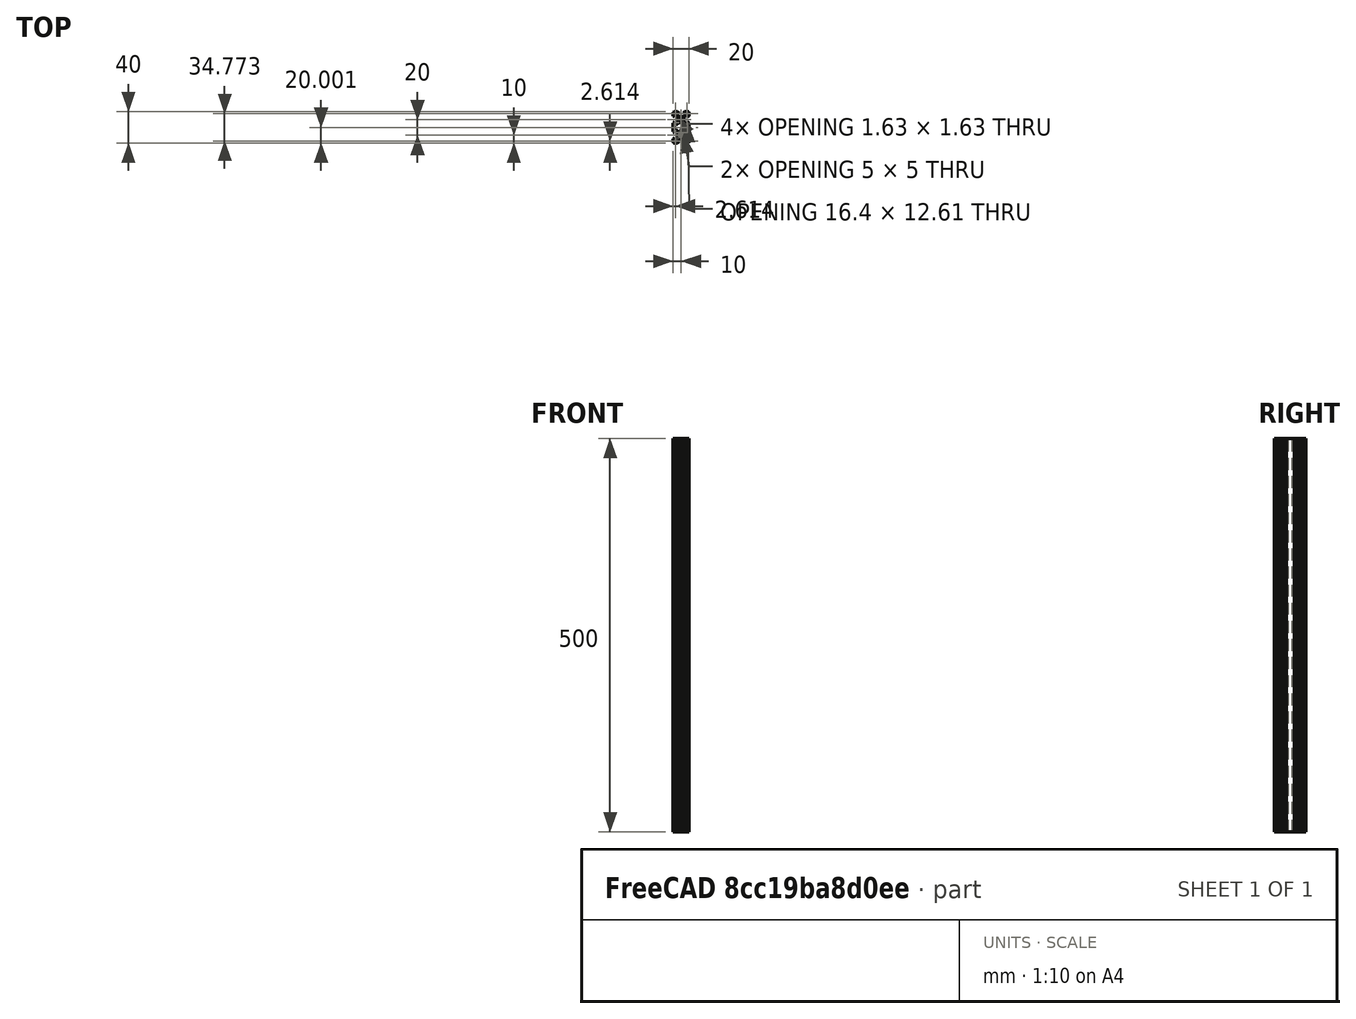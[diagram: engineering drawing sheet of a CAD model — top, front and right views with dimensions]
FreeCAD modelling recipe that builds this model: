
FCSTD DOCUMENT  (FreeCAD 0.16R6707 (Git))
Label: extrusion 20mmx40mm
License: All rights reserved
LicenseURL: http://en.wikipedia.org/wiki/All_rights_reserved
objects: Sketcher::SketchObject×1, PartDesign::Pad×1
note: 3 computed .brp shape members not serialized (recipe doc carries the construction recipe); baked Part::Feature solids carry a one-line shape summary decoded from their .brp

FEATURE [Sketcher::SketchObject] Sketch
  sketch-geometry (372):
    g0: LineSegment StartX=9.79303 StartY=6.1 StartZ=0 EndX=7.16067 EndY=6.1 EndZ=0
    g1: LineSegment StartX=10 StartY=6.30697 StartZ=0 EndX=9.79303 EndY=6.1 EndZ=0
    g2: LineSegment StartX=7.16067 StartY=6.1 StartZ=0 EndX=4.5 EndY=3.43934 EndZ=0
    g3: LineSegment StartX=10.207 StartY=6.1 StartZ=0 EndX=10 EndY=6.30697 EndZ=0
    g4: LineSegment StartX=4.5 StartY=3.43934 StartZ=0 EndX=4.5 EndY=1.8 EndZ=0
    g5: LineSegment StartX=12.8393 StartY=6.1 StartZ=0 EndX=10.207 EndY=6.1 EndZ=0
    g6: LineSegment StartX=4.5 StartY=1.8 StartZ=0 EndX=7.11338 EndY=1.8 EndZ=0
    g7: LineSegment StartX=15.5 StartY=3.43934 StartZ=0 EndX=12.8393 EndY=6.1 EndZ=0
    g8: LineSegment StartX=7.11338 StartY=1.8 StartZ=0 EndX=7.11338 EndY=1.69337 EndZ=0
    g9: LineSegment StartX=15.5 StartY=1.8 StartZ=0 EndX=15.5 EndY=3.43934 EndZ=0
    g10: LineSegment StartX=7.11338 StartY=1.69337 StartZ=0 EndX=5.59781 EndY=0.177796 EndZ=0
    g11: LineSegment StartX=12.8866 StartY=1.8 StartZ=0 EndX=15.5 EndY=1.8 EndZ=0
    g12: LineSegment StartX=5.59781 StartY=0.177796 StartZ=0 EndX=5.56881 EndY=0.150641 EndZ=0
    g13: LineSegment StartX=12.8866 StartY=1.69337 StartZ=0 EndX=12.8866 EndY=1.8 EndZ=0
    g14: LineSegment StartX=5.56881 StartY=0.150641 StartZ=0 EndX=5.53811 EndY=0.12544 EndZ=0
    g15: LineSegment StartX=14.4022 StartY=0.177796 StartZ=0 EndX=12.8866 EndY=1.69337 EndZ=0
    g16: LineSegment StartX=5.53811 StartY=0.12544 StartZ=0 EndX=5.50582 EndY=0.102301 EndZ=0
    g17: LineSegment StartX=14.4312 StartY=0.150641 StartZ=0 EndX=14.4022 EndY=0.177796 EndZ=0
    g18: LineSegment StartX=5.50582 StartY=0.102301 StartZ=0 EndX=5.47208 EndY=0.0813243 EndZ=0
    g19: LineSegment StartX=14.4619 StartY=0.12544 StartZ=0 EndX=14.4312 EndY=0.150641 EndZ=0
    g20: LineSegment StartX=5.47208 StartY=0.0813243 StartZ=0 EndX=5.43705 EndY=0.0625983 EndZ=0
    g21: LineSegment StartX=14.4942 StartY=0.102301 StartZ=0 EndX=14.4619 EndY=0.12544 EndZ=0
    g22: LineSegment StartX=5.43705 StartY=0.0625983 StartZ=0 EndX=5.40086 EndY=0.0462043 EndZ=0
    g23: LineSegment StartX=14.5279 StartY=0.0813243 StartZ=0 EndX=14.4942 EndY=0.102301 EndZ=0
    g24: LineSegment StartX=5.40086 StartY=0.0462043 StartZ=0 EndX=5.36369 EndY=0.0322113 EndZ=0
    g25: LineSegment StartX=14.563 StartY=0.0625983 StartZ=0 EndX=14.5279 EndY=0.0813243 EndZ=0
    g26: LineSegment StartX=5.36369 StartY=0.0322113 StartZ=0 EndX=5.32567 EndY=0.0206793 EndZ=0
    g27: LineSegment StartX=14.5991 StartY=0.0462043 StartZ=0 EndX=14.563 EndY=0.0625983 EndZ=0
    g28: LineSegment StartX=5.32567 StartY=0.0206793 StartZ=0 EndX=5.28699 EndY=0.0116593 EndZ=0
    g29: LineSegment StartX=14.6363 StartY=0.0322113 StartZ=0 EndX=14.5991 EndY=0.0462043 EndZ=0
    g30: LineSegment StartX=5.28699 StartY=0.0116593 StartZ=0 EndX=5.24779 EndY=0.00518829 EndZ=0
    g31: LineSegment StartX=14.6743 StartY=0.0206803 StartZ=0 EndX=14.6363 EndY=0.0322113 EndZ=0
    g32: LineSegment StartX=5.24779 StartY=0.00518829 StartZ=0 EndX=5.20826 EndY=0.00129429 EndZ=0
    g33: LineSegment StartX=14.713 StartY=0.0116593 StartZ=0 EndX=14.6743 EndY=0.0206803 EndZ=0
    g34: LineSegment StartX=5.20826 StartY=0.00129429 StartZ=0 EndX=5.16856 EndY=-4.71e-06 EndZ=0
    g35: LineSegment StartX=14.7522 StartY=0.00518829 StartZ=0 EndX=14.713 EndY=0.0116593 EndZ=0
    g36: LineSegment StartX=5.16856 StartY=-4.71e-06 StartZ=0 EndX=1.5 EndY=-4.71e-06 EndZ=0
    g37: LineSegment StartX=14.7918 StartY=0.00129529 StartZ=0 EndX=14.7522 EndY=0.00518829 EndZ=0
    g38: LineSegment StartX=1.5 StartY=-4.71e-06 StartZ=0 EndX=1.30422 EndY=0.0128283 EndZ=0
    g39: LineSegment StartX=14.8315 StartY=-4.71e-06 StartZ=0 EndX=14.7918 EndY=0.00129529 EndZ=0
    g40: LineSegment StartX=1.30422 StartY=0.0128283 StartZ=0 EndX=1.11178 EndY=0.0511063 EndZ=0
    g41: LineSegment StartX=18.5 StartY=-4.71e-06 StartZ=0 EndX=14.8315 EndY=-4.71e-06 EndZ=0
    g42: LineSegment StartX=1.11178 StartY=0.0511063 StartZ=0 EndX=0.92598 EndY=0.114176 EndZ=0
    g43: LineSegment StartX=18.6958 StartY=0.0128283 StartZ=0 EndX=18.5 EndY=-4.71e-06 EndZ=0
    g44: LineSegment StartX=0.92598 StartY=0.114176 StartZ=0 EndX=0.750005 EndY=0.200957 EndZ=0
    g45: LineSegment StartX=18.8882 StartY=0.0511063 StartZ=0 EndX=18.6958 EndY=0.0128283 EndZ=0
    g46: LineSegment StartX=0.750005 StartY=0.200957 StartZ=0 EndX=0.586863 EndY=0.309965 EndZ=0
    g47: LineSegment StartX=19.074 StartY=0.114176 StartZ=0 EndX=18.8882 EndY=0.0511063 EndZ=0
    g48: LineSegment StartX=0.586863 StartY=0.309965 StartZ=0 EndX=0.439345 EndY=0.439335 EndZ=0
    g49: LineSegment StartX=19.25 StartY=0.200957 StartZ=0 EndX=19.074 EndY=0.114176 EndZ=0
    g50: LineSegment StartX=0.439345 StartY=0.439335 StartZ=0 EndX=0.309975 EndY=0.586853 EndZ=0
    g51: LineSegment StartX=19.4131 StartY=0.309965 StartZ=0 EndX=19.25 EndY=0.200957 EndZ=0
    g52: LineSegment StartX=0.309975 StartY=0.586853 StartZ=0 EndX=0.200967 EndY=0.749995 EndZ=0
    g53: LineSegment StartX=19.5607 StartY=0.439335 StartZ=0 EndX=19.4131 EndY=0.309965 EndZ=0
    g54: LineSegment StartX=0.200967 StartY=0.749995 StartZ=0 EndX=0.114186 EndY=0.92597 EndZ=0
    g55: LineSegment StartX=19.69 StartY=0.586853 StartZ=0 EndX=19.5607 EndY=0.439335 EndZ=0
    g56: LineSegment StartX=0.114186 StartY=0.92597 StartZ=0 EndX=0.0511165 EndY=1.11177 EndZ=0
    g57: LineSegment StartX=19.799 StartY=0.749995 StartZ=0 EndX=19.69 EndY=0.586853 EndZ=0
    g58: LineSegment StartX=0.0511165 StartY=1.11177 StartZ=0 EndX=0.0128375 EndY=1.30421 EndZ=0
    g59: LineSegment StartX=19.8858 StartY=0.92597 StartZ=0 EndX=19.799 EndY=0.749995 EndZ=0
    g60: LineSegment StartX=0.0128375 StartY=1.30421 StartZ=0 EndX=4.543e-06 EndY=1.5 EndZ=0
    g61: LineSegment StartX=19.9489 StartY=1.11177 StartZ=0 EndX=19.8858 EndY=0.92597 EndZ=0
    g62: LineSegment StartX=4.543e-06 StartY=1.5 StartZ=0 EndX=5.543e-06 EndY=5.1 EndZ=0
    g63: LineSegment StartX=19.9872 StartY=1.30421 StartZ=0 EndX=19.9489 EndY=1.11177 EndZ=0
    g64: LineSegment StartX=5.543e-06 StartY=5.1 StartZ=0 EndX=0.00130454 EndY=5.20825 EndZ=0
    g65: LineSegment StartX=20 StartY=1.5 StartZ=0 EndX=19.9872 EndY=1.30421 EndZ=0
    g66: LineSegment StartX=0.00130454 StartY=5.20825 StartZ=0 EndX=0.00519854 EndY=5.24778 EndZ=0
    g67: LineSegment StartX=20 StartY=5.16855 StartZ=0 EndX=20 EndY=1.5 EndZ=0
    g68: LineSegment StartX=0.00519854 StartY=5.24778 StartZ=0 EndX=0.0116695 EndY=5.28698 EndZ=0
    g69: LineSegment StartX=19.9987 StartY=5.20825 StartZ=0 EndX=20 EndY=5.16855 EndZ=0
    g70: LineSegment StartX=0.0116695 StartY=5.28698 StartZ=0 EndX=0.0206895 EndY=5.32566 EndZ=0
    g71: LineSegment StartX=19.9948 StartY=5.24778 StartZ=0 EndX=19.9987 EndY=5.20825 EndZ=0
    g72: LineSegment StartX=0.0206895 StartY=5.32566 StartZ=0 EndX=0.0322215 EndY=5.36368 EndZ=0
    g73: LineSegment StartX=19.9883 StartY=5.28698 StartZ=0 EndX=19.9948 EndY=5.24778 EndZ=0
    g74: LineSegment StartX=0.0322215 StartY=5.36368 StartZ=0 EndX=0.0462145 EndY=5.40085 EndZ=0
    g75: LineSegment StartX=19.9793 StartY=5.32566 StartZ=0 EndX=19.9883 EndY=5.28698 EndZ=0
    g76: LineSegment StartX=0.0462145 StartY=5.40085 StartZ=0 EndX=0.0626085 EndY=5.43704 EndZ=0
    g77: LineSegment StartX=19.9678 StartY=5.36368 StartZ=0 EndX=19.9793 EndY=5.32566 EndZ=0
    g78: LineSegment StartX=0.0626085 StartY=5.43704 StartZ=0 EndX=0.0813345 EndY=5.47207 EndZ=0
    g79: LineSegment StartX=19.9538 StartY=5.40085 StartZ=0 EndX=19.9678 EndY=5.36368 EndZ=0
    g80: LineSegment StartX=0.0813345 StartY=5.47207 StartZ=0 EndX=0.102312 EndY=5.50581 EndZ=0
    g81: LineSegment StartX=19.9374 StartY=5.43704 StartZ=0 EndX=19.9538 EndY=5.40085 EndZ=0
    g82: LineSegment StartX=0.102312 StartY=5.50581 StartZ=0 EndX=0.125451 EndY=5.5381 EndZ=0
    g83: LineSegment StartX=19.9187 StartY=5.47207 StartZ=0 EndX=19.9374 EndY=5.43704 EndZ=0
    g84: LineSegment StartX=0.125451 StartY=5.5381 StartZ=0 EndX=0.150652 EndY=5.5688 EndZ=0
    g85: LineSegment StartX=19.8977 StartY=5.50581 StartZ=0 EndX=19.9187 EndY=5.47207 EndZ=0
    g86: LineSegment StartX=0.150652 StartY=5.5688 StartZ=0 EndX=0.177807 EndY=5.5978 EndZ=0
    g87: LineSegment StartX=19.8746 StartY=5.5381 StartZ=0 EndX=19.8977 EndY=5.50581 EndZ=0
    g88: LineSegment StartX=0.177807 StartY=5.5978 StartZ=0 EndX=1.69338 EndY=7.11337 EndZ=0
    g89: LineSegment StartX=19.8494 StartY=5.5688 StartZ=0 EndX=19.8746 EndY=5.5381 EndZ=0
    g90: LineSegment StartX=1.69338 StartY=7.11337 StartZ=0 EndX=1.80001 EndY=7.11337 EndZ=0
    g91: LineSegment StartX=19.8222 StartY=5.5978 StartZ=0 EndX=19.8494 EndY=5.5688 EndZ=0
    g92: LineSegment StartX=1.80001 StartY=7.11337 StartZ=0 EndX=1.8 EndY=4.5 EndZ=0
    g93: LineSegment StartX=18.3066 StartY=7.11337 StartZ=0 EndX=19.8222 EndY=5.5978 EndZ=0
    g94: LineSegment StartX=1.8 StartY=4.5 StartZ=0 EndX=3.43934 EndY=4.5 EndZ=0
    g95: LineSegment StartX=18.2 StartY=7.11337 StartZ=0 EndX=18.3066 EndY=7.11337 EndZ=0
    g96: LineSegment StartX=3.43934 StartY=4.5 StartZ=0 EndX=6.1 EndY=7.16066 EndZ=0
    g97: LineSegment StartX=18.2 StartY=4.5 StartZ=0 EndX=18.2 EndY=7.11337 EndZ=0
    g98: LineSegment StartX=6.1 StartY=7.16066 StartZ=0 EndX=6.1 EndY=9.80013 EndZ=0
    g99: LineSegment StartX=16.5607 StartY=4.5 StartZ=0 EndX=18.2 EndY=4.5 EndZ=0
    g100: LineSegment StartX=6.1 StartY=9.80013 StartZ=0 EndX=6.29987 EndY=10 EndZ=0
    g101: LineSegment StartX=13.9 StartY=7.16066 StartZ=0 EndX=16.5607 EndY=4.5 EndZ=0
    g102: LineSegment StartX=6.29987 StartY=10 StartZ=0 EndX=6.1 EndY=10.1999 EndZ=0
    g103: LineSegment StartX=13.9 StartY=9.80013 StartZ=0 EndX=13.9 EndY=7.16066 EndZ=0
    g104: LineSegment StartX=6.1 StartY=10.1999 StartZ=0 EndX=6.1 EndY=12.8393 EndZ=0
    g105: LineSegment StartX=13.7001 StartY=10 StartZ=0 EndX=13.9 EndY=9.80013 EndZ=0
    g106: LineSegment StartX=6.1 StartY=12.8393 StartZ=0 EndX=3.43934 EndY=15.5 EndZ=0
    g107: LineSegment StartX=13.9 StartY=10.1999 StartZ=0 EndX=13.7001 EndY=10 EndZ=0
    g108: LineSegment StartX=3.43934 StartY=15.5 StartZ=0 EndX=1.8 EndY=15.5 EndZ=0
    g109: LineSegment StartX=13.9 StartY=12.8393 StartZ=0 EndX=13.9 EndY=10.1999 EndZ=0
    g110: LineSegment StartX=1.8 StartY=15.5 StartZ=0 EndX=1.80001 EndY=12.8866 EndZ=0
    g111: LineSegment StartX=16.5607 StartY=15.5 StartZ=0 EndX=13.9 EndY=12.8393 EndZ=0
    g112: LineSegment StartX=1.80001 StartY=12.8866 StartZ=0 EndX=1.69338 EndY=12.8866 EndZ=0
    g113: LineSegment StartX=18.2 StartY=15.5 StartZ=0 EndX=16.5607 EndY=15.5 EndZ=0
    g114: LineSegment StartX=1.69338 StartY=12.8866 StartZ=0 EndX=0.177807 EndY=14.4022 EndZ=0
    g115: LineSegment StartX=18.2 StartY=12.8866 StartZ=0 EndX=18.2 EndY=15.5 EndZ=0
    g116: LineSegment StartX=0.177807 StartY=14.4022 StartZ=0 EndX=0.150651 EndY=14.4312 EndZ=0
    g117: LineSegment StartX=18.3066 StartY=12.8866 StartZ=0 EndX=18.2 EndY=12.8866 EndZ=0
    g118: LineSegment StartX=0.150651 StartY=14.4312 StartZ=0 EndX=0.125451 EndY=14.4619 EndZ=0
    g119: LineSegment StartX=19.8222 StartY=14.4022 StartZ=0 EndX=18.3066 EndY=12.8866 EndZ=0
    g120: LineSegment StartX=0.125451 StartY=14.4619 StartZ=0 EndX=0.102312 EndY=14.4942 EndZ=0
    g121: LineSegment StartX=19.8494 StartY=14.4312 StartZ=0 EndX=19.8222 EndY=14.4022 EndZ=0
    g122: LineSegment StartX=0.102312 StartY=14.4942 StartZ=0 EndX=0.0813345 EndY=14.5279 EndZ=0
    g123: LineSegment StartX=19.8746 StartY=14.4619 StartZ=0 EndX=19.8494 EndY=14.4312 EndZ=0
    g124: LineSegment StartX=0.0813345 StartY=14.5279 StartZ=0 EndX=0.0626085 EndY=14.563 EndZ=0
    g125: LineSegment StartX=19.8977 StartY=14.4942 StartZ=0 EndX=19.8746 EndY=14.4619 EndZ=0
    g126: LineSegment StartX=0.0626085 StartY=14.563 StartZ=0 EndX=0.0462145 EndY=14.5991 EndZ=0
    g127: LineSegment StartX=19.9187 StartY=14.5279 StartZ=0 EndX=19.8977 EndY=14.4942 EndZ=0
    g128: LineSegment StartX=0.0462145 StartY=14.5991 StartZ=0 EndX=0.0322215 EndY=14.6363 EndZ=0
    g129: LineSegment StartX=19.9374 StartY=14.563 StartZ=0 EndX=19.9187 EndY=14.5279 EndZ=0
    g130: LineSegment StartX=0.0322215 StartY=14.6363 StartZ=0 EndX=0.0206895 EndY=14.6743 EndZ=0
    g131: LineSegment StartX=19.9538 StartY=14.5991 StartZ=0 EndX=19.9374 EndY=14.563 EndZ=0
    g132: LineSegment StartX=0.0206895 StartY=14.6743 StartZ=0 EndX=0.0116695 EndY=14.713 EndZ=0
    g133: LineSegment StartX=19.9678 StartY=14.6363 StartZ=0 EndX=19.9538 EndY=14.5991 EndZ=0
    g134: LineSegment StartX=0.0116695 StartY=14.713 StartZ=0 EndX=0.00519854 EndY=14.7522 EndZ=0
    g135: LineSegment StartX=19.9793 StartY=14.6743 StartZ=0 EndX=19.9678 EndY=14.6363 EndZ=0
    g136: LineSegment StartX=0.00519854 StartY=14.7522 StartZ=0 EndX=0.00130454 EndY=14.7917 EndZ=0
    g137: LineSegment StartX=19.9883 StartY=14.713 StartZ=0 EndX=19.9793 EndY=14.6743 EndZ=0
    g138: LineSegment StartX=0.00130454 StartY=14.7917 StartZ=0 EndX=4.543e-06 EndY=14.9 EndZ=0
    g139: LineSegment StartX=19.9948 StartY=14.7522 StartZ=0 EndX=19.9883 EndY=14.713 EndZ=0
    g140: LineSegment StartX=4.543e-06 StartY=14.9 StartZ=0 EndX=5.543e-06 EndY=25.1 EndZ=0
    g141: LineSegment StartX=19.9987 StartY=14.7917 StartZ=0 EndX=19.9948 EndY=14.7522 EndZ=0
    g142: LineSegment StartX=5.543e-06 StartY=25.1 StartZ=0 EndX=0.00130454 EndY=25.2082 EndZ=0
    g143: LineSegment StartX=20 StartY=14.9 StartZ=0 EndX=19.9987 EndY=14.7917 EndZ=0
    g144: LineSegment StartX=0.00130454 StartY=25.2082 StartZ=0 EndX=0.00519854 EndY=25.2478 EndZ=0
    g145: LineSegment StartX=20 StartY=25.1 StartZ=0 EndX=20 EndY=14.9 EndZ=0
    g146: LineSegment StartX=0.00519854 StartY=25.2478 StartZ=0 EndX=0.0116695 EndY=25.287 EndZ=0
    g147: LineSegment StartX=19.9987 StartY=25.2082 StartZ=0 EndX=20 EndY=25.1 EndZ=0
    g148: LineSegment StartX=0.0116695 StartY=25.287 StartZ=0 EndX=0.0206895 EndY=25.3257 EndZ=0
    g149: LineSegment StartX=19.9948 StartY=25.2478 StartZ=0 EndX=19.9987 EndY=25.2082 EndZ=0
    g150: LineSegment StartX=0.0206895 StartY=25.3257 StartZ=0 EndX=0.0322215 EndY=25.3637 EndZ=0
    g151: LineSegment StartX=19.9883 StartY=25.287 StartZ=0 EndX=19.9948 EndY=25.2478 EndZ=0
    g152: LineSegment StartX=0.0322215 StartY=25.3637 StartZ=0 EndX=0.0462145 EndY=25.4009 EndZ=0
    g153: LineSegment StartX=19.9793 StartY=25.3257 StartZ=0 EndX=19.9883 EndY=25.287 EndZ=0
    g154: LineSegment StartX=0.0462145 StartY=25.4009 StartZ=0 EndX=0.0626085 EndY=25.437 EndZ=0
    g155: LineSegment StartX=19.9678 StartY=25.3637 StartZ=0 EndX=19.9793 EndY=25.3257 EndZ=0
    g156: LineSegment StartX=0.0626085 StartY=25.437 StartZ=0 EndX=0.0813345 EndY=25.4721 EndZ=0
    g157: LineSegment StartX=19.9538 StartY=25.4009 StartZ=0 EndX=19.9678 EndY=25.3637 EndZ=0
    g158: LineSegment StartX=0.0813345 StartY=25.4721 StartZ=0 EndX=0.102312 EndY=25.5058 EndZ=0
    g159: LineSegment StartX=19.9374 StartY=25.437 StartZ=0 EndX=19.9538 EndY=25.4009 EndZ=0
    g160: LineSegment StartX=0.102312 StartY=25.5058 StartZ=0 EndX=0.125451 EndY=25.5381 EndZ=0
    g161: LineSegment StartX=19.9187 StartY=25.4721 StartZ=0 EndX=19.9374 EndY=25.437 EndZ=0
    g162: LineSegment StartX=0.125451 StartY=25.5381 StartZ=0 EndX=0.150652 EndY=25.5688 EndZ=0
    g163: LineSegment StartX=19.8977 StartY=25.5058 StartZ=0 EndX=19.9187 EndY=25.4721 EndZ=0
    g164: LineSegment StartX=0.150652 StartY=25.5688 StartZ=0 EndX=0.177807 EndY=25.5978 EndZ=0
    g165: LineSegment StartX=19.8746 StartY=25.5381 StartZ=0 EndX=19.8977 EndY=25.5058 EndZ=0
    g166: LineSegment StartX=0.177807 StartY=25.5978 StartZ=0 EndX=1.69338 EndY=27.1134 EndZ=0
    g167: LineSegment StartX=19.8494 StartY=25.5688 StartZ=0 EndX=19.8746 EndY=25.5381 EndZ=0
    g168: LineSegment StartX=1.69338 StartY=27.1134 StartZ=0 EndX=1.80001 EndY=27.1134 EndZ=0
    g169: LineSegment StartX=19.8222 StartY=25.5978 StartZ=0 EndX=19.8494 EndY=25.5688 EndZ=0
    g170: LineSegment StartX=1.80001 StartY=27.1134 StartZ=0 EndX=1.80001 EndY=24.5 EndZ=0
    g171: LineSegment StartX=18.3066 StartY=27.1134 StartZ=0 EndX=19.8222 EndY=25.5978 EndZ=0
    g172: LineSegment StartX=1.80001 StartY=24.5 StartZ=0 EndX=3.43934 EndY=24.5 EndZ=0
    g173: LineSegment StartX=18.2 StartY=27.1134 StartZ=0 EndX=18.3066 EndY=27.1134 EndZ=0
    g174: LineSegment StartX=3.43934 StartY=24.5 StartZ=0 EndX=6.10001 EndY=27.1607 EndZ=0
    g175: LineSegment StartX=18.2 StartY=24.5 StartZ=0 EndX=18.2 EndY=27.1134 EndZ=0
    g176: LineSegment StartX=6.10001 StartY=27.1607 StartZ=0 EndX=6.10001 EndY=29.8001 EndZ=0
    g177: LineSegment StartX=16.5607 StartY=24.5 StartZ=0 EndX=18.2 EndY=24.5 EndZ=0
    g178: LineSegment StartX=6.10001 StartY=29.8001 StartZ=0 EndX=6.29987 EndY=30 EndZ=0
    g179: LineSegment StartX=13.9 StartY=27.1607 StartZ=0 EndX=16.5607 EndY=24.5 EndZ=0
    g180: LineSegment StartX=6.29987 StartY=30 StartZ=0 EndX=6.10001 EndY=30.1999 EndZ=0
    g181: LineSegment StartX=13.9 StartY=29.8001 StartZ=0 EndX=13.9 EndY=27.1607 EndZ=0
    g182: LineSegment StartX=6.10001 StartY=30.1999 StartZ=0 EndX=6.10001 EndY=32.8393 EndZ=0
    g183: LineSegment StartX=13.7001 StartY=30 StartZ=0 EndX=13.9 EndY=29.8001 EndZ=0
    g184: LineSegment StartX=6.10001 StartY=32.8393 StartZ=0 EndX=3.43935 EndY=35.5 EndZ=0
    g185: LineSegment StartX=13.9 StartY=30.1999 StartZ=0 EndX=13.7001 EndY=30 EndZ=0
    g186: LineSegment StartX=3.43935 StartY=35.5 StartZ=0 EndX=1.80001 EndY=35.5 EndZ=0
    g187: LineSegment StartX=13.9 StartY=32.8393 StartZ=0 EndX=13.9 EndY=30.1999 EndZ=0
    g188: LineSegment StartX=1.80001 StartY=35.5 StartZ=0 EndX=1.80001 EndY=32.8866 EndZ=0
    g189: LineSegment StartX=16.5607 StartY=35.5 StartZ=0 EndX=13.9 EndY=32.8393 EndZ=0
    g190: LineSegment StartX=1.80001 StartY=32.8866 StartZ=0 EndX=1.69338 EndY=32.8866 EndZ=0
    g191: LineSegment StartX=18.2 StartY=35.5 StartZ=0 EndX=16.5607 EndY=35.5 EndZ=0
    g192: LineSegment StartX=1.69338 StartY=32.8866 StartZ=0 EndX=0.177807 EndY=34.4022 EndZ=0
    g193: LineSegment StartX=18.2 StartY=32.8866 StartZ=0 EndX=18.2 EndY=35.5 EndZ=0
    g194: LineSegment StartX=0.177807 StartY=34.4022 StartZ=0 EndX=0.150652 EndY=34.4312 EndZ=0
    g195: LineSegment StartX=18.3066 StartY=32.8866 StartZ=0 EndX=18.2 EndY=32.8866 EndZ=0
    g196: LineSegment StartX=0.150652 StartY=34.4312 StartZ=0 EndX=0.125451 EndY=34.4619 EndZ=0
    g197: LineSegment StartX=19.8222 StartY=34.4022 StartZ=0 EndX=18.3066 EndY=32.8866 EndZ=0
    g198: LineSegment StartX=0.125451 StartY=34.4619 StartZ=0 EndX=0.102312 EndY=34.4942 EndZ=0
    g199: LineSegment StartX=19.8494 StartY=34.4312 StartZ=0 EndX=19.8222 EndY=34.4022 EndZ=0
    g200: LineSegment StartX=0.102312 StartY=34.4942 StartZ=0 EndX=0.0813345 EndY=34.5279 EndZ=0
    g201: LineSegment StartX=19.8746 StartY=34.4619 StartZ=0 EndX=19.8494 EndY=34.4312 EndZ=0
    g202: LineSegment StartX=0.0813345 StartY=34.5279 StartZ=0 EndX=0.0626085 EndY=34.563 EndZ=0
    g203: LineSegment StartX=19.8977 StartY=34.4942 StartZ=0 EndX=19.8746 EndY=34.4619 EndZ=0
    g204: LineSegment StartX=0.0626085 StartY=34.563 StartZ=0 EndX=0.0462145 EndY=34.5991 EndZ=0
    g205: LineSegment StartX=19.9187 StartY=34.5279 StartZ=0 EndX=19.8977 EndY=34.4942 EndZ=0
    g206: LineSegment StartX=0.0462145 StartY=34.5991 StartZ=0 EndX=0.0322215 EndY=34.6363 EndZ=0
    g207: LineSegment StartX=19.9374 StartY=34.563 StartZ=0 EndX=19.9187 EndY=34.5279 EndZ=0
    g208: LineSegment StartX=0.0322215 StartY=34.6363 StartZ=0 EndX=0.0206905 EndY=34.6743 EndZ=0
    g209: LineSegment StartX=19.9538 StartY=34.5991 StartZ=0 EndX=19.9374 EndY=34.563 EndZ=0
    g210: LineSegment StartX=0.0206905 StartY=34.6743 StartZ=0 EndX=0.0116695 EndY=34.713 EndZ=0
    g211: LineSegment StartX=19.9678 StartY=34.6363 StartZ=0 EndX=19.9538 EndY=34.5991 EndZ=0
    g212: LineSegment StartX=0.0116695 StartY=34.713 StartZ=0 EndX=0.00519854 EndY=34.7522 EndZ=0
    g213: LineSegment StartX=19.9793 StartY=34.6743 StartZ=0 EndX=19.9678 EndY=34.6363 EndZ=0
    g214: LineSegment StartX=0.00519854 StartY=34.7522 StartZ=0 EndX=0.00130554 EndY=34.7917 EndZ=0
    g215: LineSegment StartX=19.9883 StartY=34.713 StartZ=0 EndX=19.9793 EndY=34.6743 EndZ=0
    g216: LineSegment StartX=0.00130554 StartY=34.7917 StartZ=0 EndX=5.543e-06 EndY=34.9 EndZ=0
    g217: LineSegment StartX=19.9948 StartY=34.7522 StartZ=0 EndX=19.9883 EndY=34.713 EndZ=0
    g218: LineSegment StartX=5.543e-06 StartY=34.9 StartZ=0 EndX=5.543e-06 EndY=38.5 EndZ=0
    g219: LineSegment StartX=19.9987 StartY=34.7917 StartZ=0 EndX=19.9948 EndY=34.7522 EndZ=0
    g220: LineSegment StartX=5.543e-06 StartY=38.5 StartZ=0 EndX=0.0128375 EndY=38.6958 EndZ=0
    g221: LineSegment StartX=20 StartY=34.8314 StartZ=0 EndX=19.9987 EndY=34.7917 EndZ=0
    g222: LineSegment StartX=0.0128375 StartY=38.6958 StartZ=0 EndX=0.0511165 EndY=38.8882 EndZ=0
    g223: LineSegment StartX=20 StartY=38.5 StartZ=0 EndX=20 EndY=34.8314 EndZ=0
    g224: LineSegment StartX=0.0511165 StartY=38.8882 StartZ=0 EndX=0.114187 EndY=39.074 EndZ=0
    g225: LineSegment StartX=19.9872 StartY=38.6958 StartZ=0 EndX=20 EndY=38.5 EndZ=0
    g226: LineSegment StartX=0.114187 StartY=39.074 StartZ=0 EndX=0.200968 EndY=39.25 EndZ=0
    g227: LineSegment StartX=19.9489 StartY=38.8882 StartZ=0 EndX=19.9872 EndY=38.6958 EndZ=0
    g228: LineSegment StartX=0.200968 StartY=39.25 StartZ=0 EndX=0.309976 EndY=39.4131 EndZ=0
    g229: LineSegment StartX=19.8858 StartY=39.074 StartZ=0 EndX=19.9489 EndY=38.8882 EndZ=0
    g230: LineSegment StartX=0.309976 StartY=39.4131 StartZ=0 EndX=0.439346 EndY=39.5607 EndZ=0
    g231: LineSegment StartX=19.799 StartY=39.25 StartZ=0 EndX=19.8858 EndY=39.074 EndZ=0
    g232: LineSegment StartX=0.439346 StartY=39.5607 StartZ=0 EndX=0.586864 EndY=39.69 EndZ=0
    g233: LineSegment StartX=19.69 StartY=39.4131 StartZ=0 EndX=19.799 EndY=39.25 EndZ=0
    g234: LineSegment StartX=0.586864 StartY=39.69 StartZ=0 EndX=0.750006 EndY=39.799 EndZ=0
    g235: LineSegment StartX=19.5607 StartY=39.5607 StartZ=0 EndX=19.69 EndY=39.4131 EndZ=0
    g236: LineSegment StartX=0.750006 StartY=39.799 StartZ=0 EndX=0.925981 EndY=39.8858 EndZ=0
    g237: LineSegment StartX=19.4131 StartY=39.69 StartZ=0 EndX=19.5607 EndY=39.5607 EndZ=0
    g238: LineSegment StartX=0.925981 StartY=39.8858 StartZ=0 EndX=1.11178 EndY=39.9489 EndZ=0
    g239: LineSegment StartX=19.25 StartY=39.799 StartZ=0 EndX=19.4131 EndY=39.69 EndZ=0
    g240: LineSegment StartX=1.11178 StartY=39.9489 StartZ=0 EndX=1.30422 EndY=39.9872 EndZ=0
    g241: LineSegment StartX=19.074 StartY=39.8858 StartZ=0 EndX=19.25 EndY=39.799 EndZ=0
    g242: LineSegment StartX=1.30422 StartY=39.9872 StartZ=0 EndX=1.50001 EndY=40 EndZ=0
    g243: LineSegment StartX=18.8882 StartY=39.9489 StartZ=0 EndX=19.074 EndY=39.8858 EndZ=0
    g244: LineSegment StartX=1.50001 StartY=40 StartZ=0 EndX=5.16856 EndY=40 EndZ=0
    g245: LineSegment StartX=18.6958 StartY=39.9872 StartZ=0 EndX=18.8882 EndY=39.9489 EndZ=0
    g246: LineSegment StartX=5.16856 StartY=40 StartZ=0 EndX=5.20826 EndY=39.9987 EndZ=0
    g247: LineSegment StartX=18.5 StartY=40 StartZ=0 EndX=18.6958 EndY=39.9872 EndZ=0
    g248: LineSegment StartX=5.20826 StartY=39.9987 StartZ=0 EndX=5.24779 EndY=39.9948 EndZ=0
    g249: LineSegment StartX=14.8315 StartY=40 StartZ=0 EndX=18.5 EndY=40 EndZ=0
    g250: LineSegment StartX=5.24779 StartY=39.9948 StartZ=0 EndX=5.28699 EndY=39.9883 EndZ=0
    g251: LineSegment StartX=14.7918 StartY=39.9987 StartZ=0 EndX=14.8315 EndY=40 EndZ=0
    g252: LineSegment StartX=5.28699 StartY=39.9883 StartZ=0 EndX=5.32567 EndY=39.9793 EndZ=0
    g253: LineSegment StartX=14.7522 StartY=39.9948 StartZ=0 EndX=14.7918 EndY=39.9987 EndZ=0
    g254: LineSegment StartX=5.32567 StartY=39.9793 StartZ=0 EndX=5.36369 EndY=39.9678 EndZ=0
    g255: LineSegment StartX=14.713 StartY=39.9883 StartZ=0 EndX=14.7522 EndY=39.9948 EndZ=0
    g256: LineSegment StartX=5.36369 StartY=39.9678 StartZ=0 EndX=5.40086 EndY=39.9538 EndZ=0
    g257: LineSegment StartX=14.6743 StartY=39.9793 StartZ=0 EndX=14.713 EndY=39.9883 EndZ=0
    g258: LineSegment StartX=5.40086 StartY=39.9538 StartZ=0 EndX=5.43705 EndY=39.9374 EndZ=0
    g259: LineSegment StartX=14.6363 StartY=39.9678 StartZ=0 EndX=14.6743 EndY=39.9793 EndZ=0
    g260: LineSegment StartX=5.43705 StartY=39.9374 StartZ=0 EndX=5.47208 EndY=39.9187 EndZ=0
    g261: LineSegment StartX=14.5991 StartY=39.9538 StartZ=0 EndX=14.6363 EndY=39.9678 EndZ=0
    g262: LineSegment StartX=5.47208 StartY=39.9187 StartZ=0 EndX=5.50582 EndY=39.8977 EndZ=0
    g263: LineSegment StartX=14.563 StartY=39.9374 StartZ=0 EndX=14.5991 EndY=39.9538 EndZ=0
    g264: LineSegment StartX=5.50582 StartY=39.8977 StartZ=0 EndX=5.53811 EndY=39.8746 EndZ=0
    g265: LineSegment StartX=14.5279 StartY=39.9187 StartZ=0 EndX=14.563 EndY=39.9374 EndZ=0
    g266: LineSegment StartX=5.53811 StartY=39.8746 StartZ=0 EndX=5.56881 EndY=39.8493 EndZ=0
    g267: LineSegment StartX=14.4942 StartY=39.8977 StartZ=0 EndX=14.5279 EndY=39.9187 EndZ=0
    g268: LineSegment StartX=5.56881 StartY=39.8493 StartZ=0 EndX=5.59781 EndY=39.8222 EndZ=0
    g269: LineSegment StartX=14.4619 StartY=39.8746 StartZ=0 EndX=14.4942 EndY=39.8977 EndZ=0
    g270: LineSegment StartX=5.59781 StartY=39.8222 StartZ=0 EndX=7.11338 EndY=38.3066 EndZ=0
    g271: LineSegment StartX=14.4312 StartY=39.8493 StartZ=0 EndX=14.4619 EndY=39.8746 EndZ=0
    g272: LineSegment StartX=7.11338 StartY=38.3066 StartZ=0 EndX=7.11338 EndY=38.2 EndZ=0
    g273: LineSegment StartX=14.4022 StartY=39.8222 StartZ=0 EndX=14.4312 EndY=39.8493 EndZ=0
    g274: LineSegment StartX=7.11338 StartY=38.2 StartZ=0 EndX=4.50001 EndY=38.2 EndZ=0
    g275: LineSegment StartX=12.8866 StartY=38.3066 StartZ=0 EndX=14.4022 EndY=39.8222 EndZ=0
    g276: LineSegment StartX=4.50001 StartY=38.2 StartZ=0 EndX=4.50001 EndY=36.5607 EndZ=0
    g277: LineSegment StartX=12.8866 StartY=38.2 StartZ=0 EndX=12.8866 EndY=38.3066 EndZ=0
    g278: LineSegment StartX=4.50001 StartY=36.5607 StartZ=0 EndX=7.16067 EndY=33.9 EndZ=0
    g279: LineSegment StartX=15.5 StartY=38.2 StartZ=0 EndX=12.8866 EndY=38.2 EndZ=0
    g280: LineSegment StartX=7.16067 StartY=33.9 StartZ=0 EndX=9.79303 EndY=33.9 EndZ=0
    g281: LineSegment StartX=15.5 StartY=36.5607 StartZ=0 EndX=15.5 EndY=38.2 EndZ=0
    g282: LineSegment StartX=9.79303 StartY=33.9 StartZ=0 EndX=10 EndY=33.693 EndZ=0
    g283: LineSegment StartX=12.8393 StartY=33.9 StartZ=0 EndX=15.5 EndY=36.5607 EndZ=0
    g284: LineSegment StartX=10 StartY=33.693 StartZ=0 EndX=10.207 EndY=33.9 EndZ=0
    g285: LineSegment StartX=10.207 StartY=33.9 StartZ=0 EndX=12.8393 EndY=33.9 EndZ=0
    g286: LineSegment StartX=17.6576 StartY=3.42725 StartZ=0 EndX=16.5728 EndY=2.34241 EndZ=0
    g287: LineSegment StartX=18.2 StartY=3.42725 StartZ=0 EndX=17.6576 EndY=3.42725 EndZ=0
    g288: LineSegment StartX=16.5728 StartY=2.34241 StartZ=0 EndX=16.5728 EndY=1.8 EndZ=0
    g289: LineSegment StartX=18.2 StartY=1.8 StartZ=0 EndX=18.2 EndY=3.42725 EndZ=0
    g290: LineSegment StartX=16.5728 StartY=1.8 StartZ=0 EndX=18.2 EndY=1.8 EndZ=0
    g291: LineSegment StartX=10.6471 StartY=32.4148 StartZ=0 EndX=10 EndY=32.5 EndZ=0
    g292: LineSegment StartX=11.25 StartY=32.1651 StartZ=0 EndX=10.6471 EndY=32.4148 EndZ=0
    g293: LineSegment StartX=10 StartY=32.5 StartZ=0 EndX=9.35296 EndY=32.4148 EndZ=0
    g294: LineSegment StartX=11.7678 StartY=31.7678 StartZ=0 EndX=11.25 EndY=32.1651 EndZ=0
    g295: LineSegment StartX=9.35296 StartY=32.4148 StartZ=0 EndX=8.75001 EndY=32.1651 EndZ=0
    g296: LineSegment StartX=12.1651 StartY=31.25 StartZ=0 EndX=11.7678 EndY=31.7678 EndZ=0
    g297: LineSegment StartX=8.75001 StartY=32.1651 StartZ=0 EndX=8.23224 EndY=31.7678 EndZ=0
    g298: LineSegment StartX=12.4148 StartY=30.647 StartZ=0 EndX=12.1651 EndY=31.25 EndZ=0
    g299: LineSegment StartX=8.23224 StartY=31.7678 StartZ=0 EndX=7.83494 EndY=31.25 EndZ=0
    g300: LineSegment StartX=12.5 StartY=30 StartZ=0 EndX=12.4148 EndY=30.647 EndZ=0
    g301: LineSegment StartX=7.83494 StartY=31.25 StartZ=0 EndX=7.58519 EndY=30.647 EndZ=0
    g302: LineSegment StartX=12.4148 StartY=29.3529 StartZ=0 EndX=12.5 EndY=30 EndZ=0
    g303: LineSegment StartX=7.58519 StartY=30.647 StartZ=0 EndX=7.50001 EndY=30 EndZ=0
    g304: LineSegment StartX=12.1651 StartY=28.75 StartZ=0 EndX=12.4148 EndY=29.3529 EndZ=0
    g305: LineSegment StartX=7.50001 StartY=30 StartZ=0 EndX=7.58519 EndY=29.3529 EndZ=0
    g306: LineSegment StartX=11.7678 StartY=28.2322 StartZ=0 EndX=12.1651 EndY=28.75 EndZ=0
    g307: LineSegment StartX=7.58519 StartY=29.3529 StartZ=0 EndX=7.83494 EndY=28.75 EndZ=0
    g308: LineSegment StartX=11.25 StartY=27.8349 StartZ=0 EndX=11.7678 EndY=28.2322 EndZ=0
    g309: LineSegment StartX=7.83494 StartY=28.75 StartZ=0 EndX=8.23224 EndY=28.2322 EndZ=0
    g310: LineSegment StartX=10.6471 StartY=27.5852 StartZ=0 EndX=11.25 EndY=27.8349 EndZ=0
    g311: LineSegment StartX=8.23224 StartY=28.2322 StartZ=0 EndX=8.75001 EndY=27.8349 EndZ=0
    g312: LineSegment StartX=10 StartY=27.5 StartZ=0 EndX=10.6471 EndY=27.5852 EndZ=0
    g313: LineSegment StartX=8.75001 StartY=27.8349 StartZ=0 EndX=9.35296 EndY=27.5852 EndZ=0
    g314: LineSegment StartX=9.35296 StartY=27.5852 StartZ=0 EndX=10 EndY=27.5 EndZ=0
    g315: LineSegment StartX=10.207 StartY=13.9 StartZ=0 EndX=12.8393 EndY=13.9 EndZ=0
    g316: LineSegment StartX=10 StartY=13.6952 StartZ=0 EndX=10.207 EndY=13.9 EndZ=0
    g317: LineSegment StartX=12.8393 StartY=13.9 StartZ=0 EndX=16.2393 EndY=17.3 EndZ=0
    g318: LineSegment StartX=9.79303 StartY=13.9 StartZ=0 EndX=10 EndY=13.6952 EndZ=0
    g319: LineSegment StartX=16.2393 StartY=17.3 StartZ=0 EndX=18.2 EndY=17.3 EndZ=0
    g320: LineSegment StartX=7.16067 StartY=13.9 StartZ=0 EndX=9.79303 EndY=13.9 EndZ=0
    g321: LineSegment StartX=18.2 StartY=17.3 StartZ=0 EndX=18.2 EndY=22.7 EndZ=0
    g322: LineSegment StartX=3.76067 StartY=17.3 StartZ=0 EndX=7.16067 EndY=13.9 EndZ=0
    g323: LineSegment StartX=18.2 StartY=22.7 StartZ=0 EndX=16.2393 EndY=22.7 EndZ=0
    g324: LineSegment StartX=1.80001 StartY=17.3 StartZ=0 EndX=3.76067 EndY=17.3 EndZ=0
    g325: LineSegment StartX=16.2393 StartY=22.7 StartZ=0 EndX=12.8393 EndY=26.1 EndZ=0
    g326: LineSegment StartX=1.80001 StartY=22.7 StartZ=0 EndX=1.80001 EndY=17.3 EndZ=0
    g327: LineSegment StartX=12.8393 StartY=26.1 StartZ=0 EndX=10.207 EndY=26.1 EndZ=0
    g328: LineSegment StartX=3.76067 StartY=22.7 StartZ=0 EndX=1.80001 EndY=22.7 EndZ=0
    g329: LineSegment StartX=10.207 StartY=26.1 StartZ=0 EndX=10 EndY=26.307 EndZ=0
    g330: LineSegment StartX=7.16067 StartY=26.1 StartZ=0 EndX=3.76067 EndY=22.7 EndZ=0
    g331: LineSegment StartX=10 StartY=26.307 StartZ=0 EndX=9.79303 EndY=26.1 EndZ=0
    g332: LineSegment StartX=9.79303 StartY=26.1 StartZ=0 EndX=7.16067 EndY=26.1 EndZ=0
    g333: LineSegment StartX=10.6471 StartY=12.4148 StartZ=0 EndX=10 EndY=12.5 EndZ=0
    g334: LineSegment StartX=11.25 StartY=12.1651 StartZ=0 EndX=10.6471 EndY=12.4148 EndZ=0
    g335: LineSegment StartX=10 StartY=12.5 StartZ=0 EndX=9.35296 EndY=12.4148 EndZ=0
    g336: LineSegment StartX=11.7678 StartY=11.7678 StartZ=0 EndX=11.25 EndY=12.1651 EndZ=0
    g337: LineSegment StartX=9.35296 StartY=12.4148 StartZ=0 EndX=8.75 EndY=12.1651 EndZ=0
    g338: LineSegment StartX=12.1651 StartY=11.25 StartZ=0 EndX=11.7678 EndY=11.7678 EndZ=0
    g339: LineSegment StartX=8.75 StartY=12.1651 StartZ=0 EndX=8.23224 EndY=11.7678 EndZ=0
    g340: LineSegment StartX=12.4148 StartY=10.647 StartZ=0 EndX=12.1651 EndY=11.25 EndZ=0
    g341: LineSegment StartX=8.23224 StartY=11.7678 StartZ=0 EndX=7.83494 EndY=11.25 EndZ=0
    g342: LineSegment StartX=12.5 StartY=10 StartZ=0 EndX=12.4148 EndY=10.647 EndZ=0
    g343: LineSegment StartX=7.83494 StartY=11.25 StartZ=0 EndX=7.58519 EndY=10.647 EndZ=0
    g344: LineSegment StartX=12.4148 StartY=9.35295 StartZ=0 EndX=12.5 EndY=10 EndZ=0
    g345: LineSegment StartX=7.58519 StartY=10.647 StartZ=0 EndX=7.5 EndY=10 EndZ=0
    g346: LineSegment StartX=12.1651 StartY=8.75 StartZ=0 EndX=12.4148 EndY=9.35295 EndZ=0
    g347: LineSegment StartX=7.5 StartY=10 StartZ=0 EndX=7.58519 EndY=9.35295 EndZ=0
    g348: LineSegment StartX=11.7678 StartY=8.23223 StartZ=0 EndX=12.1651 EndY=8.75 EndZ=0
    g349: LineSegment StartX=7.58519 StartY=9.35295 StartZ=0 EndX=7.83494 EndY=8.75 EndZ=0
    g350: LineSegment StartX=11.25 StartY=7.83493 StartZ=0 EndX=11.7678 EndY=8.23223 EndZ=0
    g351: LineSegment StartX=7.83494 StartY=8.75 StartZ=0 EndX=8.23224 EndY=8.23223 EndZ=0
    g352: LineSegment StartX=10.6471 StartY=7.58518 StartZ=0 EndX=11.25 EndY=7.83493 EndZ=0
    g353: LineSegment StartX=8.23224 StartY=8.23223 StartZ=0 EndX=8.75 EndY=7.83493 EndZ=0
    g354: LineSegment StartX=10 StartY=7.5 StartZ=0 EndX=10.6471 EndY=7.58518 EndZ=0
    g355: LineSegment StartX=8.75 StartY=7.83493 StartZ=0 EndX=9.35296 EndY=7.58518 EndZ=0
    g356: LineSegment StartX=9.35296 StartY=7.58518 StartZ=0 EndX=10 EndY=7.5 EndZ=0
    g357: LineSegment StartX=18.2 StartY=36.5727 StartZ=0 EndX=18.2 EndY=38.2 EndZ=0
    g358: LineSegment StartX=17.6576 StartY=36.5727 StartZ=0 EndX=18.2 EndY=36.5727 EndZ=0
    g359: LineSegment StartX=18.2 StartY=38.2 StartZ=0 EndX=16.5728 EndY=38.2 EndZ=0
    g360: LineSegment StartX=16.5728 StartY=37.6576 StartZ=0 EndX=17.6576 EndY=36.5727 EndZ=0
    g361: LineSegment StartX=16.5728 StartY=38.2 StartZ=0 EndX=16.5728 EndY=37.6576 EndZ=0
    g362: LineSegment StartX=3.42726 StartY=2.34241 StartZ=0 EndX=2.34242 EndY=3.42725 EndZ=0
    g363: LineSegment StartX=3.42726 StartY=1.8 StartZ=0 EndX=3.42726 EndY=2.34241 EndZ=0
    g364: LineSegment StartX=2.34242 StartY=3.42725 StartZ=0 EndX=1.80001 EndY=3.42725 EndZ=0
    g365: LineSegment StartX=1.80001 StartY=1.8 StartZ=0 EndX=3.42726 EndY=1.8 EndZ=0
    g366: LineSegment StartX=1.80001 StartY=3.42725 StartZ=0 EndX=1.80001 EndY=1.8 EndZ=0
    g367: LineSegment StartX=3.42726 StartY=38.2 StartZ=0 EndX=1.80001 EndY=38.2 EndZ=0
    g368: LineSegment StartX=3.42726 StartY=37.6576 StartZ=0 EndX=3.42726 EndY=38.2 EndZ=0
    g369: LineSegment StartX=1.80001 StartY=38.2 StartZ=0 EndX=1.80001 EndY=36.5727 EndZ=0
    g370: LineSegment StartX=2.34242 StartY=36.5727 StartZ=0 EndX=3.42726 EndY=37.6576 EndZ=0
    g371: LineSegment StartX=1.80001 StartY=36.5727 StartZ=0 EndX=2.34242 EndY=36.5727 EndZ=0
FEATURE [PartDesign::Pad] Pad
  Length = 500
  Length2 = 100
  Sketch = -> Sketch
  Type = 0
